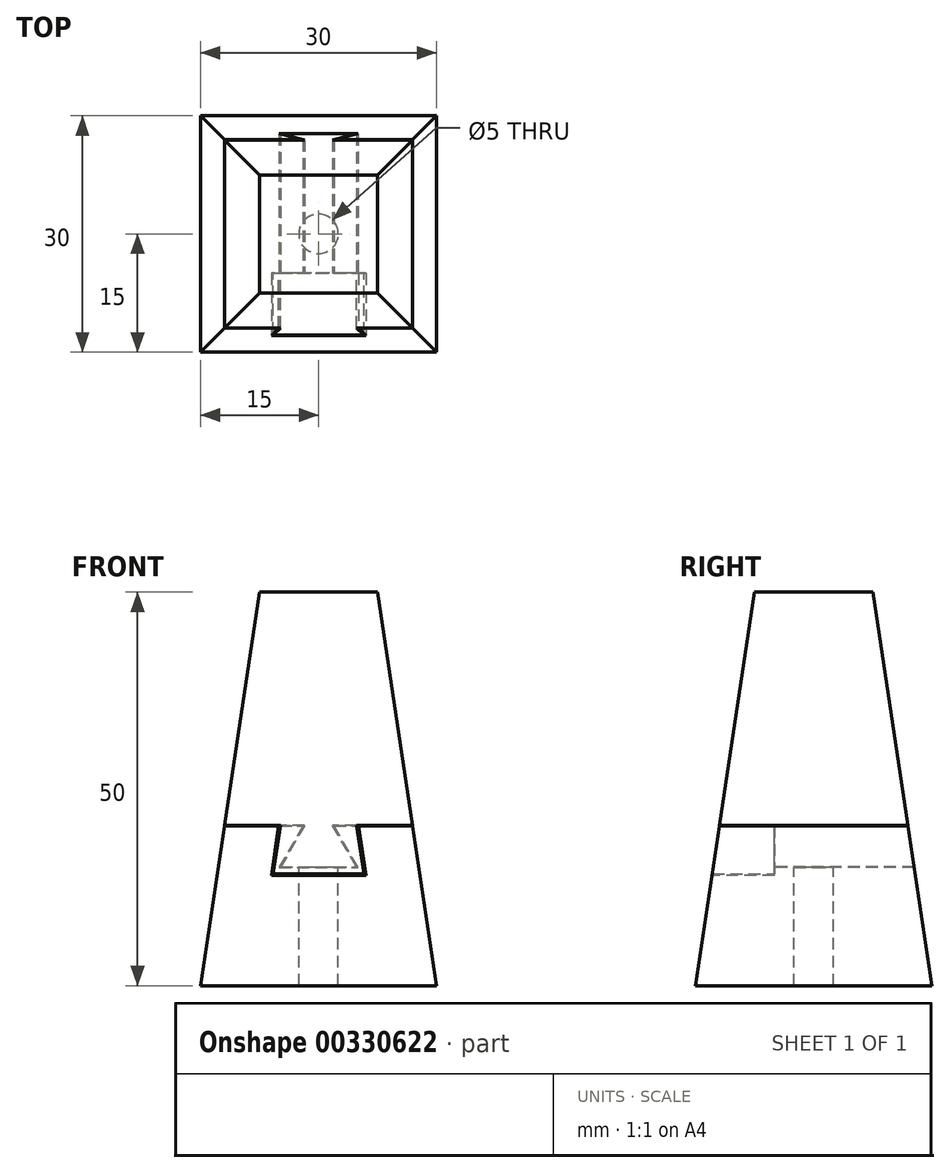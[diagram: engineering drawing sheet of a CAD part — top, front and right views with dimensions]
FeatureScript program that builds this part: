
annotation { "Feature Type Name" : "Feature", "Feature Type Description" : "" }
export const myFeature = defineFeature(function(context is Context, id is Id, definition is map)
    precondition{}
    {
        {
            var Q0;
            Q0=qCreatedBy(makeId("Top.planeOp"),FACE);
            var sketch = newSketch(context, id + "F0", { "sketchPlane" : qUnion([Q0])});
            skLineSegment(sketch, "E0.bottom", {"start": v(15, 15) * mm, "end": v(-15, 15) * mm});
            skLineSegment(sketch, "E0.top", {"start": v(15, -15) * mm, "end": v(-15, -15) * mm});
            skLineSegment(sketch, "E0.left", {"start": v(15, 15) * mm, "end": v(15, -15) * mm});
            skLineSegment(sketch, "E0.right", {"start": v(-15, 15) * mm, "end": v(-15, -15) * mm});
            skPoint(sketch, "E0.middle", {"position": v(0, 0) * mm});
            skSolve(sketch);
        }
        {
            var Q0;
            Q0=qCreatedBy(makeId("Top.planeOp"),FACE);
            cPlane(context, id + "F1", {"entities" : qUnion([Q0]), "cplaneType" : CPlaneType.OFFSET, "offset" : 50 * mm, "width" : 150 * mm, "height" : 150 * mm});
        }
        {
            var Q0;
            Q0=qCreatedBy(id+"F1.planeOp",FACE);
            var sketch = newSketch(context, id + "F2", { "sketchPlane" : qUnion([Q0])});
            skLineSegment(sketch, "E1.bottom", {"start": v(7.5, 7.5) * mm, "end": v(-7.5, 7.5) * mm});
            skLineSegment(sketch, "E1.top", {"start": v(7.5, -7.5) * mm, "end": v(-7.5, -7.5) * mm});
            skLineSegment(sketch, "E1.left", {"start": v(7.5, 7.5) * mm, "end": v(7.5, -7.5) * mm});
            skLineSegment(sketch, "E1.right", {"start": v(-7.5, 7.5) * mm, "end": v(-7.5, -7.5) * mm});
            skPoint(sketch, "E1.middle", {"position": v(0, 0) * mm});
            skSolve(sketch);
        }
        {
            var Q0;
            Q0=makeQuery(id+"F0.imprint","IMPRINT",FACE,{"disambiguationData":[TD([[makeQuery(id+"F0.imprint","IMPRINT",EDGE,{"derivedFrom":sQuery(id+"F0.wireOp",EDGE,"E0.bottom")}),1.0]])]});
            var Q1;
            Q1=makeQuery(id+"F2.imprint","IMPRINT",FACE,{"disambiguationData":[TD([[makeQuery(id+"F2.imprint","IMPRINT",EDGE,{"derivedFrom":sQuery(id+"F2.wireOp",EDGE,"E1.bottom")}),1.0]])]});
            loft(context, id + "F3", {"sheetProfilesArray" : [{ "sheetProfileEntities" : qUnion([Q0]) }, { "sheetProfileEntities" : qUnion([Q1]) }]});
        }
        {
            var Q0;
            Q0=qCreatedBy(makeId("Front.planeOp"),FACE);
            var sketch = newSketch(context, id + "F4", { "sketchPlane" : qUnion([Q0])});
            skLineSegment(sketch, "E2.0.0", {"start": v(-15, 0) * mm, "end": v(-7.5, 50) * mm, "construction": true});
            skLineSegment(sketch, "E2.0.1", {"start": v(-7.5, 50) * mm, "end": v(7.5, 50) * mm, "construction": true});
            skLineSegment(sketch, "E2.0.2", {"start": v(7.5, 50) * mm, "end": v(15, 0) * mm, "construction": true});
            skLineSegment(sketch, "E2.0.3", {"start": v(15, 0) * mm, "end": v(-15, 0) * mm, "construction": true});
            skLineSegment(sketch, "E3", {"start": v(11.96, 20.27) * mm, "end": v(1.96, 20.27) * mm});
            skLineSegment(sketch, "E4", {"start": v(1.96, 20.27) * mm, "end": v(5, 15) * mm});
            skLineSegment(sketch, "E5", {"start": v(5, 15) * mm, "end": v(-5, 15) * mm});
            skLineSegment(sketch, "E6", {"start": v(-5, 15) * mm, "end": v(-1.96, 20.27) * mm});
            skLineSegment(sketch, "E7", {"start": v(-1.96, 20.27) * mm, "end": v(-11.96, 20.27) * mm});
            skLineSegment(sketch, "E8.0", {"start": v(-1.79, 20.37) * mm, "end": v(-11.96, 20.37) * mm});
            skLineSegment(sketch, "E8.1", {"start": v(11.96, 20.37) * mm, "end": v(1.79, 20.37) * mm});
            skLineSegment(sketch, "E8.2", {"start": v(1.79, 20.37) * mm, "end": v(4.83, 15.1) * mm});
            skLineSegment(sketch, "E8.3", {"start": v(4.83, 15.1) * mm, "end": v(-4.83, 15.1) * mm});
            skLineSegment(sketch, "E8.4", {"start": v(-4.83, 15.1) * mm, "end": v(-1.79, 20.37) * mm});
            skLineSegment(sketch, "E9", {"start": v(11.96, 20.37) * mm, "end": v(11.96, 20.27) * mm});
            skLineSegment(sketch, "E10", {"start": v(-11.96, 20.37) * mm, "end": v(-11.96, 20.27) * mm});
            skSolve(sketch);
        }
        {
            var Q0;
            Q0 = qSketchRegion(id + "F4", true);
            extrude(context, id + "F5", {"entities" : qUnion([Q0]), "operationType" : NewBodyOperationType.REMOVE, "endBound" : BoundingType.THROUGH_ALL, "oppositeDirection" : true, "depth" : 25 * mm, "hasSecondDirection" : true, "secondDirectionBound" : SecondDirectionBoundingType.THROUGH_ALL, "secondDirectionOppositeDirection" : false, "secondDirectionDepth" : 25 * mm});
        }
        {
            var Q0;
            Q0=qCreatedBy(makeId("Front.planeOp"),FACE);
            cPlane(context, id + "F6", {"entities" : qUnion([Q0]), "cplaneType" : CPlaneType.OFFSET, "offset" : 15 * mm, "width" : 150 * mm, "height" : 150 * mm});
        }
        {
            var Q0;
            Q0=qCreatedBy(id+"F6.planeOp",FACE);
            var sketch = newSketch(context, id + "F7", { "sketchPlane" : qUnion([Q0])});
            skLineSegment(sketch, "E11.0", {"start": v(11.95, 20.37) * mm, "end": v(1.79, 20.37) * mm, "construction": true});
            skLineSegment(sketch, "E12.0", {"start": v(-1.79, 20.37) * mm, "end": v(-11.95, 20.37) * mm, "construction": true});
            skLineSegment(sketch, "E13.0.1", {"start": v(-4.83, 15.1) * mm, "end": v(-1.79, 20.37) * mm, "construction": true});
            skLineSegment(sketch, "E13.0.2", {"start": v(4.83, 15.1) * mm, "end": v(-4.83, 15.1) * mm, "construction": true});
            skLineSegment(sketch, "E13.0.3", {"start": v(1.79, 20.37) * mm, "end": v(4.83, 15.1) * mm, "construction": true});
            skLineSegment(sketch, "E13.0.5", {"start": v(11.95, 20.37) * mm, "end": v(7.5, 50) * mm, "construction": true});
            skLineSegment(sketch, "E13.0.6", {"start": v(-7.5, 50) * mm, "end": v(7.5, 50) * mm, "construction": true});
            skLineSegment(sketch, "E13.0.7", {"start": v(-7.5, 50) * mm, "end": v(-11.95, 20.37) * mm, "construction": true});
            skLineSegment(sketch, "E14.0.0", {"start": v(-5, 15) * mm, "end": v(-1.96, 20.27) * mm, "construction": true});
            skLineSegment(sketch, "E14.0.1", {"start": v(-1.96, 20.27) * mm, "end": v(-11.96, 20.27) * mm, "construction": true});
            skLineSegment(sketch, "E14.0.2", {"start": v(-11.96, 20.27) * mm, "end": v(-15, 0) * mm, "construction": true});
            skLineSegment(sketch, "E14.0.3", {"start": v(-15, 0) * mm, "end": v(15, 0) * mm, "construction": true});
            skLineSegment(sketch, "E14.0.4", {"start": v(15, 0) * mm, "end": v(11.96, 20.27) * mm, "construction": true});
            skLineSegment(sketch, "E14.0.5", {"start": v(11.96, 20.27) * mm, "end": v(1.96, 20.27) * mm, "construction": true});
            skLineSegment(sketch, "E14.0.6", {"start": v(1.96, 20.27) * mm, "end": v(5, 15) * mm, "construction": true});
            skLineSegment(sketch, "E14.0.7", {"start": v(5, 15) * mm, "end": v(-5, 15) * mm, "construction": true});
            skLineSegment(sketch, "E15", {"start": v(-5.05, 20.37) * mm, "end": v(5.05, 20.37) * mm});
            skLineSegment(sketch, "E16", {"start": v(5.05, 20.37) * mm, "end": v(6, 14) * mm});
            skLineSegment(sketch, "E17", {"start": v(6, 14) * mm, "end": v(-6, 14) * mm});
            skLineSegment(sketch, "E18", {"start": v(-6, 14) * mm, "end": v(-5.05, 20.37) * mm});
            skSolve(sketch);
        }
        {
            var Q0;
            Q0 = qSketchRegion(id + "F7", true);
            extrude(context, id + "F8", {"entities" : qUnion([Q0]), "operationType" : NewBodyOperationType.REMOVE, "oppositeDirection" : true, "depth" : 10 * mm});
        }
        {
            var Q0;
            {var subQ0=sQuery(id+"F7.wireOp",EDGE,"E15");Q0=makeQuery(id+"F8.boolean.opBoolean","COPY",FACE,{"disambiguationData":[TD([makeQuery(id+"F5.boolean.opBoolean","COPY",FACE,{"derivedFrom":makeQuery(id+"F5.opExtrude","SWEPT_FACE",FACE,{"disambiguationData":[OSD([sQuery(id+"F4.wireOp",EDGE,"E8.0")])]})})])],"derivedFrom":makeQuery(id+"F8.opExtrude","CAP_FACE",FACE,{"disambiguationData":[OSD([subQ0,sQuery(id+"F7.wireOp",EDGE,"E16"),sQuery(id+"F7.wireOp",EDGE,"E17"),sQuery(id+"F7.wireOp",EDGE,"E18")])],"isStart":false})});}
            var sketch = newSketch(context, id + "F9", { "sketchPlane" : qUnion([Q0])});
            skLineSegment(sketch, "E19.0", {"start": v(-5.77, 14.2) * mm, "end": v(-4.86, 20.24) * mm});
            skLineSegment(sketch, "E19.1", {"start": v(5.77, 14.2) * mm, "end": v(-5.77, 14.2) * mm});
            skLineSegment(sketch, "E19.2", {"start": v(4.86, 20.24) * mm, "end": v(5.77, 14.2) * mm});
            skLineSegment(sketch, "E20.0.0", {"start": v(11.95, 20.37) * mm, "end": v(-11.95, 20.37) * mm, "construction": true});
            skLineSegment(sketch, "E20.0.1", {"start": v(11.95, 20.37) * mm, "end": v(7.5, 50) * mm, "construction": true});
            skLineSegment(sketch, "E20.0.2", {"start": v(-7.5, 50) * mm, "end": v(7.5, 50) * mm, "construction": true});
            skLineSegment(sketch, "E20.0.3", {"start": v(-7.5, 50) * mm, "end": v(-11.95, 20.37) * mm, "construction": true});
            skLineSegment(sketch, "E21", {"start": v(-4.86, 20.24) * mm, "end": v(-4.84, 20.37) * mm});
            skLineSegment(sketch, "E22", {"start": v(4.86, 20.24) * mm, "end": v(4.84, 20.37) * mm});
            skLineSegment(sketch, "E23", {"start": v(4.84, 20.37) * mm, "end": v(-4.84, 20.37) * mm});
            skSolve(sketch);
        }
        {
            var Q0;
            Q0 = qSketchRegion(id + "F9", true);
            var Q1;
            {var subQ1=sQuery(id+"F2.wireOp",EDGE,"E1.top");var subQ2=sQuery(id+"F2.wireOp",EDGE,"E1.left");var subQ3=sQuery(id+"F2.wireOp",EDGE,"E1.right");var subQ4=sQuery(id+"F0.wireOp",EDGE,"E0.right");var subQ5=sQuery(id+"F0.wireOp",EDGE,"E0.top");var subQ7=sQuery(id+"F0.wireOp",EDGE,"E0.left");Q1=makeQuery(id+"F5.boolean.opBoolean","SPLIT",FACE,{"disambiguationData":[TD([makeQuery(id+"F5.opExtrude","SWEPT_FACE",FACE,{"disambiguationData":[OSD([sQuery(id+"F4.wireOp",EDGE,"E8.0")])]})])],"derivedFrom":makeQuery(id+"F3.opLoft","SWEPT_FACE",FACE,{"disambiguationData":[OSD([subQ5,subQ7,subQ4,subQ1,subQ2,subQ3])]})});}
            extrude(context, id + "F10", {"entities" : qUnion([Q0]), "operationType" : NewBodyOperationType.ADD, "endBound" : BoundingType.UP_TO_SURFACE, "endBoundEntityFace" : qUnion([Q1]), "depth" : 25 * mm});
        }
        {
            var Q0;
            Q0=makeQuery(id+"F5.boolean.opBoolean","COPY",FACE,{"derivedFrom":makeQuery(id+"F5.opExtrude","SWEPT_FACE",FACE,{"disambiguationData":[OSD([sQuery(id+"F4.wireOp",EDGE,"E5")])]})});
            var sketch = newSketch(context, id + "F11", { "sketchPlane" : qUnion([Q0])});
            skCircle(sketch, "E24", {"center": v(0, 0) * mm, "radius": 2.5 * mm});
            skSolve(sketch);
        }
        {
            var Q0;
            Q0 = qSketchRegion(id + "F11", true);
            extrude(context, id + "F12", {"entities" : qUnion([Q0]), "operationType" : NewBodyOperationType.REMOVE, "endBound" : BoundingType.THROUGH_ALL, "oppositeDirection" : true, "depth" : 25 * mm});
        }
    });
